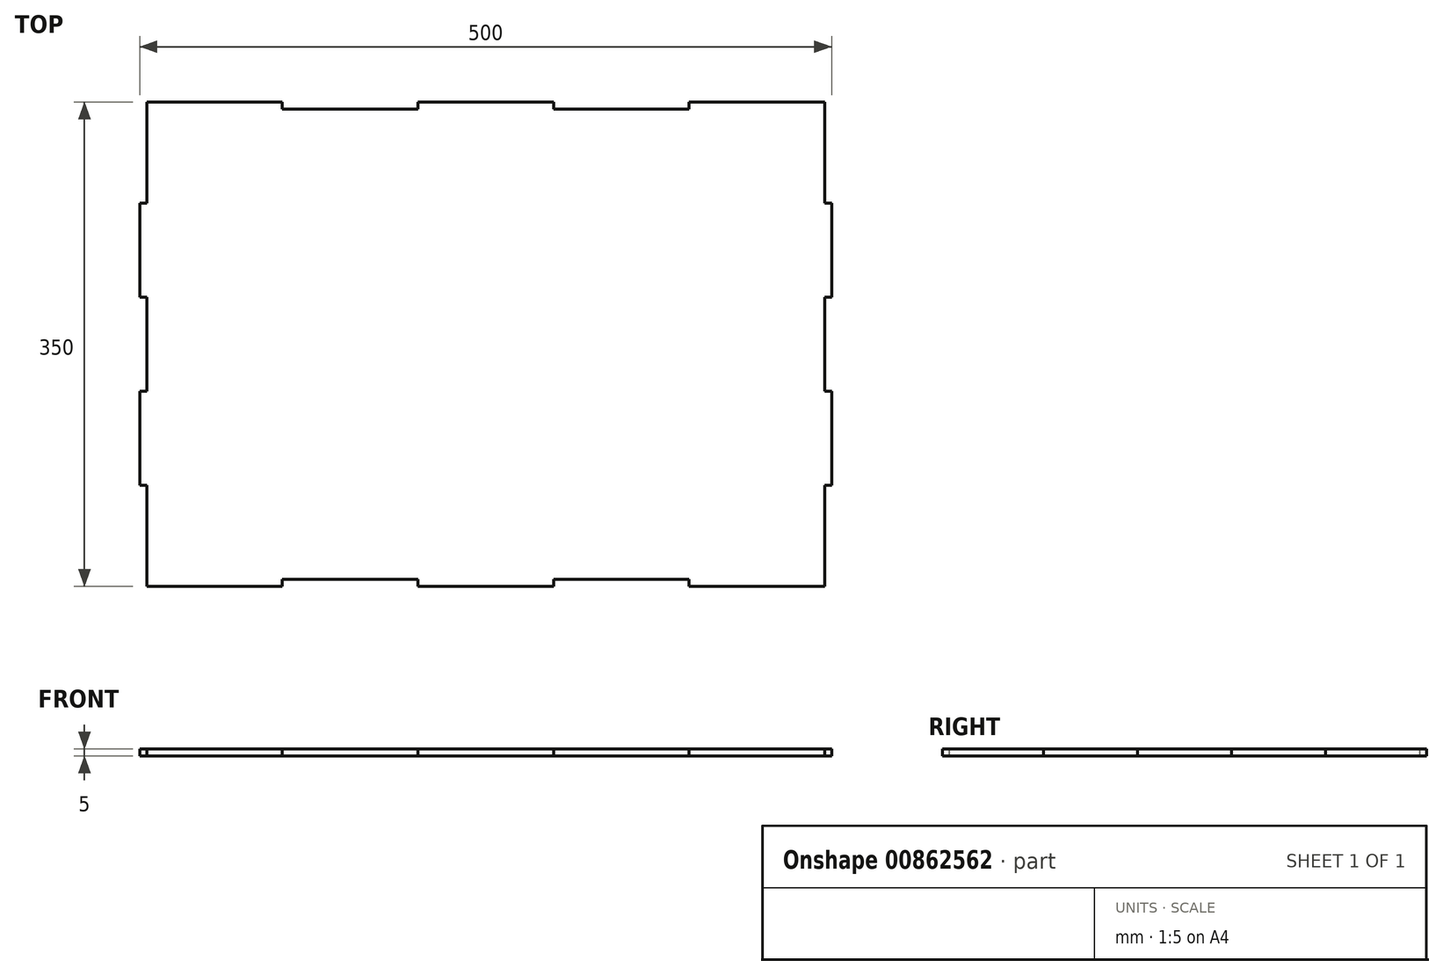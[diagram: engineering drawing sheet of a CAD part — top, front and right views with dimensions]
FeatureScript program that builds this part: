
annotation { "Feature Type Name" : "Feature", "Feature Type Description" : "" }
export const myFeature = defineFeature(function(context is Context, id is Id, definition is map)
    precondition{}
    {
        {
            var Q0;
            Q0=qCreatedBy(makeId("Top.planeOp"),FACE);
            var sketch = newSketch(context, id + "F0", { "sketchPlane" : qUnion([Q0])});
            skLineSegment(sketch, "E0.bottom", {"start": v(245, -170) * mm, "end": v(-245, -170) * mm});
            skLineSegment(sketch, "E0.top", {"start": v(245, 170) * mm, "end": v(-245, 170) * mm});
            skLineSegment(sketch, "E0.left", {"start": v(245, -170) * mm, "end": v(245, 170) * mm});
            skLineSegment(sketch, "E0.right", {"start": v(-245, -170) * mm, "end": v(-245, 170) * mm});
            skPoint(sketch, "E0.middle", {"position": v(0, 0) * mm});
            skLineSegment(sketch, "E1", {"start": v(-245, -170) * mm, "end": v(-245, -175) * mm});
            skLineSegment(sketch, "E2", {"start": v(-245, -175) * mm, "end": v(-147, -175) * mm});
            skLineSegment(sketch, "E3", {"start": v(-147, -175) * mm, "end": v(-147, -170) * mm});
            skLineSegment(sketch, "E4", {"start": v(-552.17, 0) * mm, "end": v(393.12, 0) * mm});
            skLineSegment(sketch, "E5", {"start": v(0, -308.05) * mm, "end": v(0, 300.63) * mm});
            skLineSegment(sketch, "E6.MirrorCS", {"start": v(-245, 170) * mm, "end": v(-245, 175) * mm});
            skLineSegment(sketch, "E7.MirrorCS", {"start": v(-245, 175) * mm, "end": v(-147, 175) * mm});
            skLineSegment(sketch, "E8.MirrorCS", {"start": v(-147, 175) * mm, "end": v(-147, 170) * mm});
            skLineSegment(sketch, "E9.1.0.0", {"start": v(-49, 170) * mm, "end": v(-49, 175) * mm});
            skLineSegment(sketch, "E9.1.0.1", {"start": v(-49, 175) * mm, "end": v(49, 175) * mm});
            skLineSegment(sketch, "E9.1.0.2", {"start": v(49, 175) * mm, "end": v(49, 170) * mm});
            skLineSegment(sketch, "E9.1.0.3", {"start": v(-49, -170) * mm, "end": v(-49, -175) * mm});
            skLineSegment(sketch, "E9.1.0.4", {"start": v(-49, -175) * mm, "end": v(49, -175) * mm});
            skLineSegment(sketch, "E9.1.0.5", {"start": v(49, -175) * mm, "end": v(49, -170) * mm});
            skLineSegment(sketch, "E9.2.0.0", {"start": v(147, 170) * mm, "end": v(147, 175) * mm});
            skLineSegment(sketch, "E9.2.0.1", {"start": v(147, 175) * mm, "end": v(245, 175) * mm});
            skLineSegment(sketch, "E9.2.0.2", {"start": v(245, 175) * mm, "end": v(245, 170) * mm});
            skLineSegment(sketch, "E9.2.0.3", {"start": v(147, -170) * mm, "end": v(147, -175) * mm});
            skLineSegment(sketch, "E9.2.0.4", {"start": v(147, -175) * mm, "end": v(245, -175) * mm});
            skLineSegment(sketch, "E9.2.0.5", {"start": v(245, -175) * mm, "end": v(245, -170) * mm});
            skLineSegment(sketch, "E9.direction1", {"start": v(-245, 170) * mm, "end": v(-49, 170) * mm, "construction": true});
            skLineSegment(sketch, "E10", {"start": v(245, 102) * mm, "end": v(250, 102) * mm});
            skLineSegment(sketch, "E11", {"start": v(250, 102) * mm, "end": v(250, 34) * mm});
            skLineSegment(sketch, "E12", {"start": v(250, 34) * mm, "end": v(245, 34) * mm});
            skLineSegment(sketch, "E13.MirrorCS", {"start": v(-245, 102) * mm, "end": v(-250, 102) * mm});
            skLineSegment(sketch, "E14.MirrorCS", {"start": v(-250, 102) * mm, "end": v(-250, 34) * mm});
            skLineSegment(sketch, "E15.MirrorCS", {"start": v(-250, 34) * mm, "end": v(-245, 34) * mm});
            skLineSegment(sketch, "E16.MirrorCS", {"start": v(-245, -102) * mm, "end": v(-250, -102) * mm});
            skLineSegment(sketch, "E17.MirrorCS", {"start": v(-250, -102) * mm, "end": v(-250, -34) * mm});
            skLineSegment(sketch, "E18.MirrorCS", {"start": v(-250, -34) * mm, "end": v(-245, -34) * mm});
            skLineSegment(sketch, "E19.MirrorCS", {"start": v(245, -102) * mm, "end": v(250, -102) * mm});
            skLineSegment(sketch, "E20.MirrorCS", {"start": v(250, -102) * mm, "end": v(250, -34) * mm});
            skLineSegment(sketch, "E21.MirrorCS", {"start": v(250, -34) * mm, "end": v(245, -34) * mm});
            skSolve(sketch);
        }
        {
            var Q0;
            Q0=qSketchRegion(id+"F0",true);
            extrude(context, id + "F1", {"entities" : qUnion([Q0]), "depth" : 5 * mm, "offsetDistance" : 25 * mm});
        }
    });
